# Revit family: Hager-IC-IP40-Transparent_Door_1Row-syst-PL-en
name_source: partatom
category: Electrical Equipment
units: mm (PartAtom-declared; Revit-internal decimal feet)

## family parameters
Cut with Voids When Loaded = No
Host = Face
Panel Configuration = Two Columns, Circuits Across
Part Type = Panelboard
Room Calculation Point = No
Round Connector Dimension = Use Diameter
Shared = No

## types (8) — shared parameters
Classification.Uniclass.Pr.Description = Control circuit device enclosures
Classification.Uniclass.Pr.Number = Pr_80_77_28_16
EF000007 - Colour = EV000202 - White
EF000049 - Depth = 91 mm  [stored 0.298556 ft]
EF000116 - RAL-number = 9010
EF000118 - With mounting plate = No
EF000266 - Number of rows = 1
EF000339 - Type of cover = EV004216 - Door
EF001062 - EMC-version = No
EF001088 - Extension possible = Yes
EF001131 - Internal depth = 72 mm  [stored 0.23622 ft]
EF001134 - DIN-rail = Yes
EF001596 - Material housing = EV000139 - Plastic
EF004462 - Type of closure = EV000154 - Other
EF005474 - Degree of protection (IP) = EV006415 - IP40
EF006244 - Transparent cover/door = Yes
EF006306 - With lock = No
EF009212 - Cover model = EV000116 - Closed
EF015776 - Earthing terminal block = Yes
EF015777 - Neutral terminal block = Yes
EF015941 - Signal passing door = Yes
Ground Bus = No
HG000002 - With door or cover = Yes
HG000003 - Range = IC
HG000005 - Thickness = 3 mm  [stored 0.00984252 ft]
HG000017 - Distance between poles = 18 mm  [stored 0.0590551 ft]
Manufacturer = Hager
Neutral Bus = No
Type Comments = IC
zero-valued in all types: Default Elevation

## per-type parameters (varying)
| type | EF000003 - Mounting method | EF000008 - Width | EF000040 - Height | EF000218 - Built-in depth | EF000332 - Built-in height | EF000846 - Built-in width | EF002950 - Width in number of modular spacings | HG000004 - Manufacturer reference | HG000006 - Flush mounted | Model |
| Recessed mounted IP40 W236 H206 D91.4 8 Modular spacings - VR108TP | EV000383 - Flush mounted (plaster) | 236 mm | 206 mm  [stored 0.675853 ft] | 72 mm  [stored 0.23622 ft] | 188 mm  [stored 0.616798 ft] | 218 mm  [stored 0.715223 ft] | 8 | VR108TP | Yes | VR108TP |
| Recessed mounted IP40 W308 H226 D91.4 12 Modular spacings - VR112TP | EV000383 - Flush mounted (plaster) | 308 mm  [stored 1.0105 ft] | 226 mm  [stored 0.74147 ft] | 72 mm  [stored 0.23622 ft] | 208 mm | 290 mm  [stored 0.951444 ft] | 12 | VR112TP | Yes | VR112TP |
| Recessed mounted IP40 W416 H226 D91.4 18 Modular spacings - VR118TP | EV000383 - Flush mounted (plaster) | 416 mm | 226 mm  [stored 0.74147 ft] | 72 mm  [stored 0.23622 ft] | 208 mm | 398 mm  [stored 1.30577 ft] | 18 | VR118TP | Yes | VR118TP |
| Surface mounted IP40 W134.5 H170 D91 6 Modular spacings - VD106TP | EV000384 - Surface mounted (plaster) | 134 mm | 170 mm  [stored 0.557743 ft] | 0 mm  [stored 0 ft] | 0 mm  [stored 0 ft] | 0 mm  [stored 0 ft] | 6 | VD106TP | No | VD106TP |
| Surface mounted IP40 W170.5 H170 D91 8 Modular spacings - VD108TP | EV000384 - Surface mounted (plaster) | 170 mm  [stored 0.557743 ft] | 170 mm  [stored 0.557743 ft] | 0 mm  [stored 0 ft] | 0 mm  [stored 0 ft] | 0 mm  [stored 0 ft] | 8 | VD108TP | No | VD108TP |
| Surface mounted IP40 W206.5 H170 D91 10 Modular spacings - VD110TP | EV000384 - Surface mounted (plaster) | 206 mm  [stored 0.675853 ft] | 170 mm  [stored 0.557743 ft] | 0 mm  [stored 0 ft] | 0 mm  [stored 0 ft] | 0 mm  [stored 0 ft] | 10 | VD110TP | No | VD110TP |
| Surface mounted IP40 W292.5 H200 D91 12 Modular spacings - VD112TP | EV000384 - Surface mounted (plaster) | 292 mm  [stored 0.958005 ft] | 200 mm  [stored 0.656168 ft] | 0 mm  [stored 0 ft] | 0 mm  [stored 0 ft] | 0 mm  [stored 0 ft] | 12 | VD112TP | No | VD112TP |
| Surface mounted IP40 W400 H200 D91 18 Modular spacings - VD118TP | EV000384 - Surface mounted (plaster) | 400 mm  [stored 1.31234 ft] | 200 mm  [stored 0.656168 ft] | 0 mm  [stored 0 ft] | 0 mm  [stored 0 ft] | 0 mm  [stored 0 ft] | 18 | VD118TP | No | VD118TP |

note: [stored X ft] marks values corroborated as IEEE doubles in the binary element streams (Revit-internal decimal feet)

## geometry (parser evidence)
native form markers: Blend x4, Sweep x9
no freeform markers — native parametric forms only
